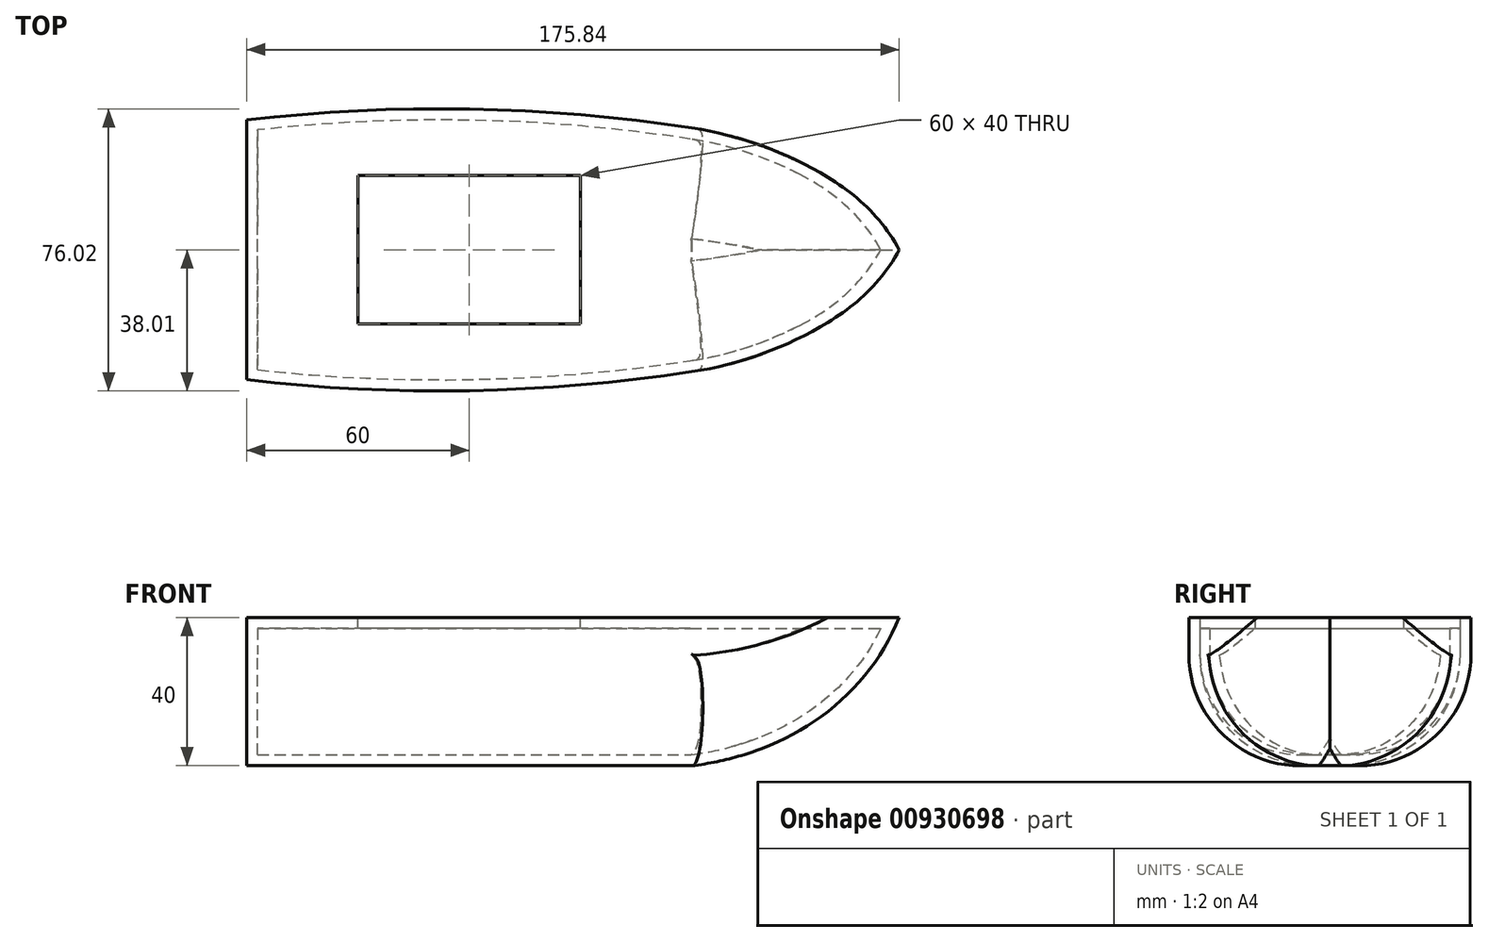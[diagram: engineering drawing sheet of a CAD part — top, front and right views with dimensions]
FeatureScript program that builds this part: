
annotation { "Feature Type Name" : "Feature", "Feature Type Description" : "" }
export const myFeature = defineFeature(function(context is Context, id is Id, definition is map)
    precondition{}
    {
        {
            var Q0;
            Q0=qCreatedBy(makeId("Top.planeOp"),FACE);
            var sketch = newSketch(context, id + "F0", { "sketchPlane" : qUnion([Q0])});
            skLineSegment(sketch, "E0", {"start": v(0, 0) * mm, "end": v(0, -35) * mm});
            skArc(sketch, "E1", {"start": v(0, -35) * mm, "mid": v(60.07, -37.94) * mm, "end": v(120, -32.84) * mm});
            skArc(sketch, "E2", {"start": v(120, -32.84) * mm, "mid": v(152.9, -21.7) * mm, "end": v(180, 0) * mm});
            skLineSegment(sketch, "E3.MirrorCS", {"start": v(0, 0) * mm, "end": v(0, 35) * mm});
            skArc(sketch, "E4.MirrorCS", {"start": v(0, 35) * mm, "mid": v(60.07, 37.94) * mm, "end": v(120, 32.84) * mm});
            skArc(sketch, "E5.MirrorCS", {"start": v(120, 32.84) * mm, "mid": v(152.9, 21.7) * mm, "end": v(180, 0) * mm});
            skSolve(sketch);
        }
        {
            var Q0;
            Q0=makeQuery(id+"F0.imprint","IMPRINT",FACE,{"disambiguationData":[TD([[makeQuery(id+"F0.imprint","IMPRINT",EDGE,{"derivedFrom":sQuery(id+"F0.wireOp",EDGE,"E0")}),1.0]])]});
            extrude(context, id + "F1", {"entities" : qUnion([Q0]), "depth" : 40 * mm, "offsetDistance" : 25 * mm});
        }
        {
            var Q0;
            Q0=qCreatedBy(makeId("Front.planeOp"),FACE);
            var sketch = newSketch(context, id + "F2", { "sketchPlane" : qUnion([Q0])});
            skArc(sketch, "E6", {"start": v(120, 0) * mm, "mid": v(154.76, 12.86) * mm, "end": v(180, 40) * mm});
            skLineSegment(sketch, "E7", {"start": v(180, 40) * mm, "end": v(180, 0) * mm});
            skLineSegment(sketch, "E8", {"start": v(180, 0) * mm, "end": v(120, 0) * mm});
            skSolve(sketch);
        }
        {
            var Q0;
            Q0 = qSketchRegion(id + "F2", true);
            extrude(context, id + "F3", {"entities" : qUnion([Q0]), "operationType" : NewBodyOperationType.REMOVE, "endBound" : BoundingType.THROUGH_ALL, "oppositeDirection" : true, "depth" : 25 * mm, "offsetDistance" : 25 * mm, "hasSecondDirection" : true, "secondDirectionBound" : SecondDirectionBoundingType.THROUGH_ALL, "secondDirectionOppositeDirection" : false, "secondDirectionDepth" : 25 * mm});
        }
        {
            var Q0;
            Q0=makeQuery(id+"F3.boolean.opBoolean","INTERSECT",EDGE,{"derivedFrom":[makeQuery(id+"F1.opExtrude","SWEPT_FACE",FACE,{"disambiguationData":[OSD([sQuery(id+"F0.wireOp",EDGE,"E2")])]}),makeQuery(id+"F3.opExtrude","SWEPT_FACE",FACE,{"disambiguationData":[OSD([sQuery(id+"F2.wireOp",EDGE,"E6")])]})]});
            var Q1;
            Q1=makeQuery(id+"F1.opExtrude","CAP_EDGE",EDGE,{"disambiguationData":[OSD([sQuery(id+"F0.wireOp",EDGE,"E1")])],"isStart":true});
            var Q2;
            Q2=makeQuery(id+"F3.boolean.opBoolean","INTERSECT",EDGE,{"derivedFrom":[makeQuery(id+"F1.opExtrude","SWEPT_FACE",FACE,{"disambiguationData":[OSD([sQuery(id+"F0.wireOp",EDGE,"E5.MirrorCS")])]}),makeQuery(id+"F3.opExtrude","SWEPT_FACE",FACE,{"disambiguationData":[OSD([sQuery(id+"F2.wireOp",EDGE,"E6")])]})]});
            var Q3;
            Q3=makeQuery(id+"F1.opExtrude","CAP_EDGE",EDGE,{"disambiguationData":[OSD([sQuery(id+"F0.wireOp",EDGE,"E4.MirrorCS")])],"isStart":true});
            fillet(context, id + "F4", {"entities" : qUnion([Q0, Q1, Q2, Q3]), "radius" : 30 * mm, "tangentPropagation" : true, "allowEdgeOverflow" : false});
        }
        {
            var Q0;
            Q0=makeQuery(id+"F1.opExtrude","CAP_FACE",FACE,{"disambiguationData":[OSD([sQuery(id+"F0.wireOp",EDGE,"E0"),sQuery(id+"F0.wireOp",EDGE,"E1"),sQuery(id+"F0.wireOp",EDGE,"E2"),sQuery(id+"F0.wireOp",EDGE,"E3.MirrorCS"),sQuery(id+"F0.wireOp",EDGE,"E4.MirrorCS"),sQuery(id+"F0.wireOp",EDGE,"E5.MirrorCS")])],"isStart":false});
            var Q1;
            Q1=makeQuery(id+"F1.opExtrude","SWEPT_BODY",BODY,{"disambiguationData":[OSD([sQuery(id+"F0.wireOp",EDGE,"E0"),sQuery(id+"F0.wireOp",EDGE,"E1"),sQuery(id+"F0.wireOp",EDGE,"E2"),sQuery(id+"F0.wireOp",EDGE,"E3.MirrorCS"),sQuery(id+"F0.wireOp",EDGE,"E4.MirrorCS"),sQuery(id+"F0.wireOp",EDGE,"E5.MirrorCS")])]});
            shell(context, id + "F5", {"isHollow" : true, "entities" : qUnion([Q0]), "parts" : qUnion([Q1]), "thickness" : 3 * mm});
        }
        {
            var Q0;
            Q0=makeQuery(id+"F1.opExtrude","CAP_FACE",FACE,{"disambiguationData":[OSD([sQuery(id+"F0.wireOp",EDGE,"E0"),sQuery(id+"F0.wireOp",EDGE,"E1"),sQuery(id+"F0.wireOp",EDGE,"E2"),sQuery(id+"F0.wireOp",EDGE,"E3.MirrorCS"),sQuery(id+"F0.wireOp",EDGE,"E4.MirrorCS"),sQuery(id+"F0.wireOp",EDGE,"E5.MirrorCS")])],"isStart":false});
            var sketch = newSketch(context, id + "F6", { "sketchPlane" : qUnion([Q0])});
            skLineSegment(sketch, "E9.bottom", {"start": v(30, 20) * mm, "end": v(90, 20) * mm});
            skLineSegment(sketch, "E9.top", {"start": v(30, -20) * mm, "end": v(90, -20) * mm});
            skLineSegment(sketch, "E9.left", {"start": v(30, 20) * mm, "end": v(30, -20) * mm});
            skLineSegment(sketch, "E9.right", {"start": v(90, 20) * mm, "end": v(90, -20) * mm});
            skPoint(sketch, "E9.middle", {"position": v(60, 0) * mm});
            skSolve(sketch);
        }
        {
            var Q0;
            Q0=makeQuery(id+"F6.imprint","IMPRINT",FACE,{"disambiguationData":[TD([[makeQuery(id+"F6.imprint","IMPRINT",EDGE,{"derivedFrom":sQuery(id+"F6.wireOp",EDGE,"E9.bottom")}),-1.0]])]});
            extrude(context, id + "F7", {"entities" : qUnion([Q0]), "operationType" : NewBodyOperationType.REMOVE, "endBound" : BoundingType.UP_TO_NEXT, "oppositeDirection" : true, "depth" : 25 * mm, "offsetDistance" : 25 * mm});
        }
    });
